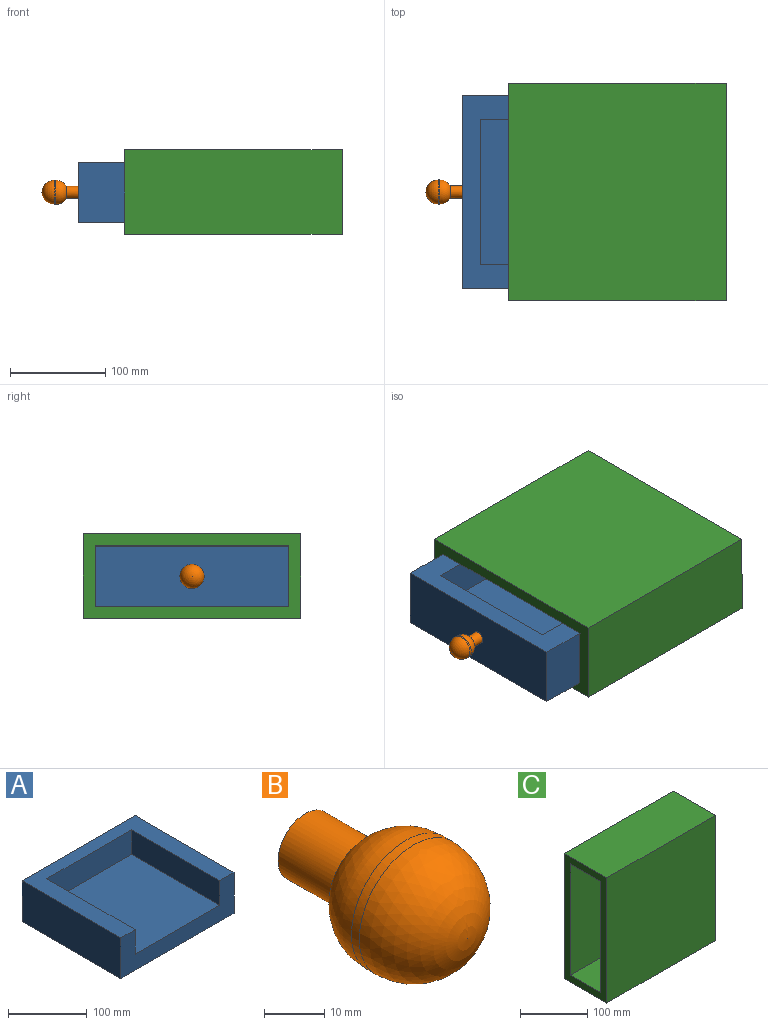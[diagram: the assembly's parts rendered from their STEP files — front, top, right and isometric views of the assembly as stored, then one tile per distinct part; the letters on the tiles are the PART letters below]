
ASSEMBLY  parts=3 mates=2
PART A: 13 faces, bbox 203.4x177.8x63.5 mm
  f0: plane 50.8x0.24mm, normal (0,-1,0), area 12mm2, adj f2,f4,f5,f9
  f1: plane 152.4x38.1mm, normal (0,-1,0), area 5806.4mm2, adj f5,f6,f7,f8
  f2: plane 19.23x0.24mm, normal (0,0,-1), area 4.5mm2, adj f0,f3,f4,f9
  f3: plane 203.44x63.5mm, normal (0,1,0), area 12915.2mm2, adj f2,f4,f5,f9,f10,f11
  f4: plane 50.8x19.23mm, normal (1,0,0), area 976.9mm2, adj f0,f2,f3,f5
  f5: plane 203.44x177.8mm, normal (0,0,1), area 11967.3mm2, adj f0,f1,f3,f4,f7,f8,f9,f10
  f6: plane 158.57x152.4mm, normal (0,0,1), area 24166.2mm2, adj f1,f7,f8,f12
  f7: plane 158.57x38.1mm, normal (1,0,0), area 6041.5mm2, adj f1,f5,f6,f12
  f8: plane 158.57x38.1mm, normal (-1,0,0), area 6041.5mm2, adj f1,f5,f6,f12
  f9: plane 177.8x63.5mm, normal (1,0,0), area 10313.4mm2, adj f0,f2,f3,f5,f11,f12
  f10: plane 177.8x63.5mm, normal (-1,0,0), area 11290.3mm2, adj f3,f5,f11,f12
  f11: plane 203.2x177.8mm, normal (0,0,-1), area 36129mm2, adj f3,f9,f10,f12
  f12: plane 203.2x63.5mm, normal (0,-1,0), area 7096.8mm2, adj f5,f6,f7,f8,f9,f10,f11
PART B: 5 faces, bbox 25.4x38.1x25.4 mm
  f0: cylinder r=12.7mm len=25.4mm, axis (0,1,0), area 147.6mm2, adj f3,f4
  f1: cylinder r=6.35mm len=12.7mm, axis (0,-1,0), area 506.7mm2, adj f2,f3
  f2: plane 12.7x12.7mm, normal (0,1,0), area 126.7mm2, adj f1
  f3: bspline ~25.4x25.4mm, area 879.7mm2, adj f0,f1
  f4: sphere r=12.7mm, area 1013.4mm2, adj f0
PART C: 15 faces, bbox 228.6x88.9x228.6 mm
  f0: plane 203.2x11.68mm, normal (0,1,0), area 2374.2mm2, adj f1,f7,f8,f11
  f1: plane 228.6x88.9mm, normal (-1,0,0), area 7419.3mm2, adj f0,f2,f4,f5,f6,f7,f8,f9
  f2: plane 228.6x88.9mm, normal (0,0,-1), area 20322.5mm2, adj f1,f3,f5,f6
  f3: plane 228.6x88.9mm, normal (1,0,0), area 20322.5mm2, adj f2,f4,f5,f6
  f4: plane 228.6x88.9mm, normal (0,0,1), area 20322.5mm2, adj f1,f3,f5,f6
  f5: plane 228.6x228.6mm, normal (0,-1,0), area 52258mm2, adj f1,f2,f3,f4
  f6: plane 228.6x228.6mm, normal (0,1,0), area 52258mm2, adj f1,f2,f3,f4
  f7: plane 216.92x63.84mm, normal (0,0,-1), area 13808.8mm2, adj f0,f1,f9,f10,f11,f12,f13,f14
  f8: plane 216.92x63.84mm, normal (0,0,1), area 13808.8mm2, adj f0,f1,f9,f10,f11,f12,f13,f14
  f9: plane 203.2x114.3mm, normal (0,-1,0), area 23225.8mm2, adj f1,f7,f8,f10
  f10: plane 203.2x0.34mm, normal (-1,0,0), area 68.7mm2, adj f7,f8,f9,f12
  f11: plane 203.2x0.34mm, normal (1,0,0), area 68.7mm2, adj f0,f7,f8,f13
  f12: plane 203.2x102.62mm, normal (0,-1,0), area 20851.6mm2, adj f7,f8,f10,f14
  f13: plane 205.23x203.2mm, normal (0,1,0), area 41703.1mm2, adj f7,f8,f11,f14
  f14: plane 203.2x63.5mm, normal (-1,0,0), area 12903.2mm2, adj f7,f8,f12,f13
PLACE A rot(axis=(0,0,1),90deg) t=(-304.61,-12.31,69.65)mm
PLACE B rot(axis=(0,0,-1),90deg) t=(-317.31,-12.21,88.7)mm
PLACE C rot(axis=(1,0,0),90deg) t=(-141.63,-12.21,133.49)mm
MATE slider A.f3 <-> C.f14  axis (-1,0,0) through (-304.61,-12.21,88.7)mm
MATE fastened B.f1 <-> A.f3  axis (1,0,0) through (-304.61,-12.21,88.7)mm
